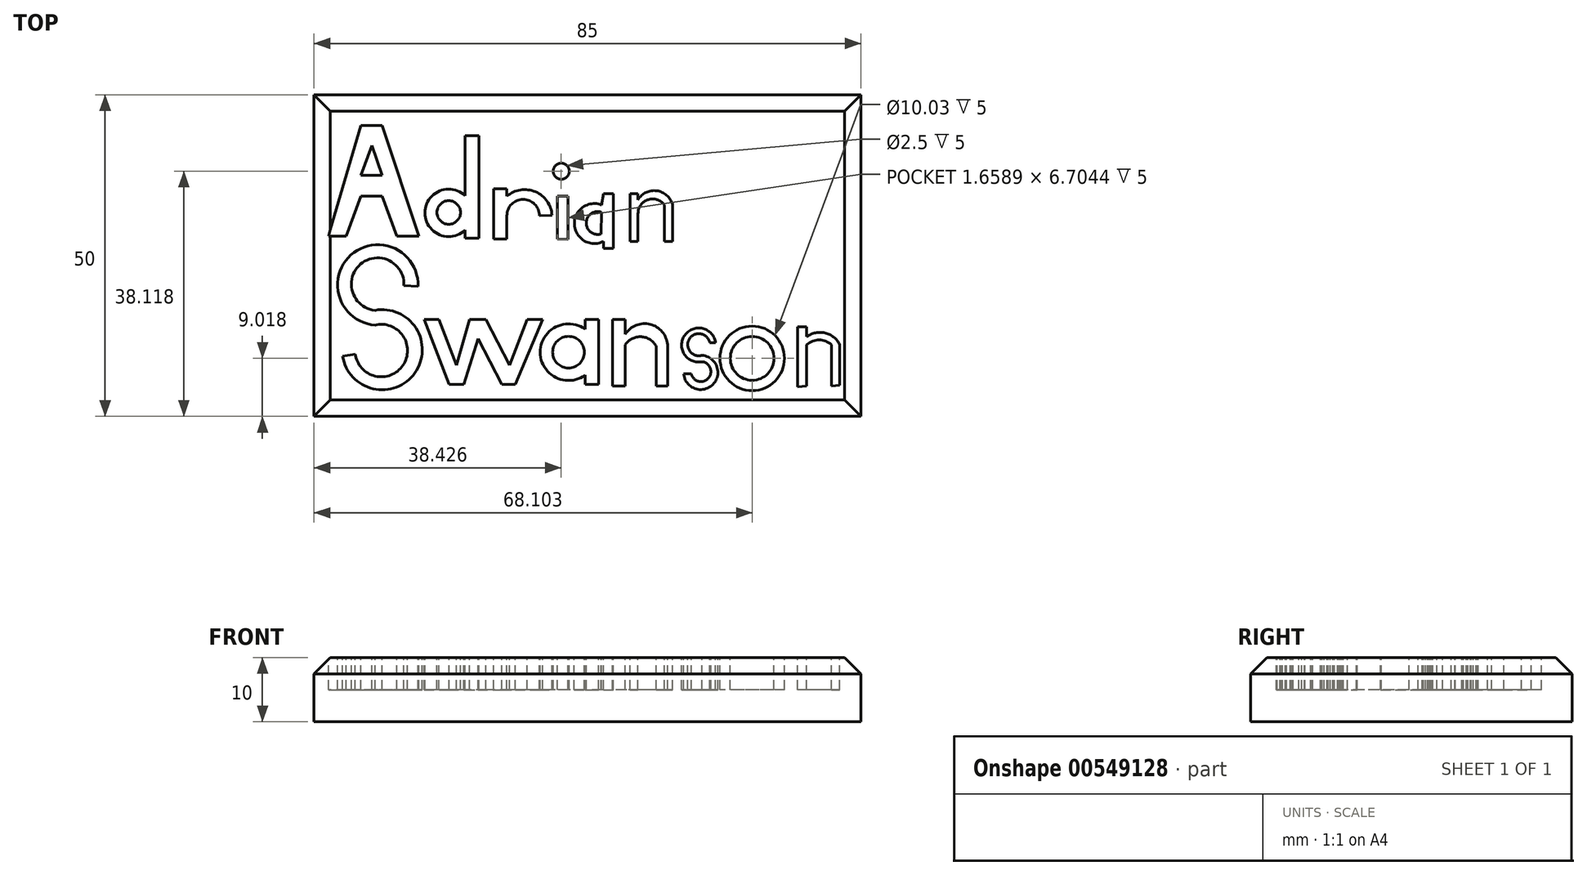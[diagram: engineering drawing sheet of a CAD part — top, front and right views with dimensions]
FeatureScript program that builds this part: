
annotation { "Feature Type Name" : "Feature", "Feature Type Description" : "" }
export const myFeature = defineFeature(function(context is Context, id is Id, definition is map)
    precondition{}
    {
        {
            var Q0;
            Q0=qCreatedBy(makeId("Top.planeOp"),FACE);
            var sketch = newSketch(context, id + "F0", { "sketchPlane" : qUnion([Q0])});
            skLineSegment(sketch, "E0", {"start": v(-29.18, 47.31) * mm, "end": v(55.82, 47.31) * mm});
            skLineSegment(sketch, "E1", {"start": v(-29.18, 47.31) * mm, "end": v(-29.18, -2.69) * mm});
            skLineSegment(sketch, "E2", {"start": v(55.82, 47.31) * mm, "end": v(55.82, -2.69) * mm});
            skLineSegment(sketch, "E3", {"start": v(-29.18, -2.69) * mm, "end": v(55.82, -2.69) * mm});
            skSolve(sketch);
        }
        {
            var Q0;
            Q0 = qSketchRegion(id + "F0", true);
            extrude(context, id + "F1", {"entities" : qUnion([Q0]), "depth" : 10 * mm, "offsetDistance" : 25.4 * mm});
        }
        {
            var Q0;
            Q0=makeQuery(id+"F1.opExtrude","CAP_FACE",FACE,{"disambiguationData":[OSD([sQuery(id+"F0.wireOp",EDGE,"E0"),sQuery(id+"F0.wireOp",EDGE,"E1"),sQuery(id+"F0.wireOp",EDGE,"E2"),sQuery(id+"F0.wireOp",EDGE,"E3")])],"isStart":false});
            var sketch = newSketch(context, id + "F2", { "sketchPlane" : qUnion([Q0])});
            skLineSegment(sketch, "E4", {"start": v(-26.94, 25.33) * mm, "end": v(-24.2, 25.33) * mm});
            skLineSegment(sketch, "E5", {"start": v(-24.2, 25.33) * mm, "end": v(-21.92, 31.56) * mm});
            skLineSegment(sketch, "E6", {"start": v(-21.92, 31.56) * mm, "end": v(-18.62, 31.56) * mm});
            skLineSegment(sketch, "E7", {"start": v(-18.62, 31.56) * mm, "end": v(-16.34, 25.33) * mm});
            skLineSegment(sketch, "E8", {"start": v(-16.34, 25.33) * mm, "end": v(-12.91, 25.33) * mm});
            skLineSegment(sketch, "E9", {"start": v(-12.91, 25.33) * mm, "end": v(-18.62, 42.52) * mm});
            skLineSegment(sketch, "E10", {"start": v(-18.62, 42.52) * mm, "end": v(-21.92, 42.52) * mm});
            skLineSegment(sketch, "E11", {"start": v(-21.92, 42.52) * mm, "end": v(-26.94, 25.33) * mm});
            skLineSegment(sketch, "E12", {"start": v(-18.62, 34.8) * mm, "end": v(-21.92, 34.8) * mm});
            skLineSegment(sketch, "E13", {"start": v(-21.92, 34.8) * mm, "end": v(-20.2, 39.41) * mm});
            skLineSegment(sketch, "E14", {"start": v(-20.2, 39.41) * mm, "end": v(-18.62, 34.8) * mm});
            skCircle(sketch, "E15", {"center": v(-8.25, 29) * mm, "radius": 1.83 * mm});
            skLineSegment(sketch, "E16", {"start": v(-5.68, 26.27) * mm, "end": v(-5.68, 25.02) * mm});
            skLineSegment(sketch, "E17", {"start": v(-5.68, 25.02) * mm, "end": v(-3.56, 25.02) * mm});
            skLineSegment(sketch, "E18", {"start": v(-3.56, 25.02) * mm, "end": v(-3.56, 40.93) * mm});
            skLineSegment(sketch, "E19", {"start": v(-3.56, 40.93) * mm, "end": v(-5.68, 40.93) * mm});
            skLineSegment(sketch, "E20", {"start": v(-5.68, 40.93) * mm, "end": v(-5.68, 31.62) * mm});
            skArc(sketch, "E21", {"start": v(-5.68, 31.62) * mm, "mid": v(-11.94, 28.95) * mm, "end": v(-5.68, 26.27) * mm});
            skLineSegment(sketch, "E22", {"start": v(-1.25, 24.89) * mm, "end": v(0.8, 24.89) * mm});
            skLineSegment(sketch, "E23", {"start": v(0.8, 24.89) * mm, "end": v(0.8, 28.52) * mm});
            skLineSegment(sketch, "E24", {"start": v(-1.25, 24.89) * mm, "end": v(-1.25, 32.68) * mm});
            skLineSegment(sketch, "E25", {"start": v(-1.25, 32.68) * mm, "end": v(0.8, 32.68) * mm});
            skLineSegment(sketch, "E26", {"start": v(0.8, 32.68) * mm, "end": v(0.8, 31.52) * mm});
            skArc(sketch, "E27", {"start": v(5.85, 28.52) * mm, "mid": v(3.32, 31.05) * mm, "end": v(0.8, 28.52) * mm});
            skArc(sketch, "E28", {"start": v(7.8, 28.54) * mm, "mid": v(5.23, 32.22) * mm, "end": v(0.8, 31.52) * mm});
            skLineSegment(sketch, "E29", {"start": v(5.85, 28.52) * mm, "end": v(7.8, 28.54) * mm});
            skLineSegment(sketch, "E30", {"start": v(8.63, 31.56) * mm, "end": v(8.63, 24.89) * mm});
            skLineSegment(sketch, "E31", {"start": v(8.63, 24.89) * mm, "end": v(10.29, 24.85) * mm});
            skLineSegment(sketch, "E32", {"start": v(10.29, 24.85) * mm, "end": v(10.29, 31.56) * mm});
            skLineSegment(sketch, "E33", {"start": v(10.29, 31.56) * mm, "end": v(8.63, 31.56) * mm});
            skCircle(sketch, "E34", {"center": v(9.25, 35.43) * mm, "radius": 1.25 * mm});
            skArc(sketch, "E35", {"start": v(15.52, 30.18) * mm, "mid": v(11.28, 27.12) * mm, "end": v(15.83, 24.53) * mm});
            skArc(sketch, "E36", {"start": v(15.52, 29.05) * mm, "mid": v(13.14, 27.43) * mm, "end": v(15.42, 25.66) * mm});
            skLineSegment(sketch, "E37", {"start": v(15.52, 29.05) * mm, "end": v(15.42, 25.66) * mm});
            skLineSegment(sketch, "E38", {"start": v(15.83, 24.53) * mm, "end": v(15.83, 23.4) * mm});
            skLineSegment(sketch, "E39", {"start": v(15.83, 23.4) * mm, "end": v(17.37, 23.4) * mm});
            skLineSegment(sketch, "E40", {"start": v(17.37, 23.4) * mm, "end": v(17.37, 31.93) * mm});
            skLineSegment(sketch, "E41", {"start": v(17.37, 31.93) * mm, "end": v(15.83, 31.93) * mm});
            skLineSegment(sketch, "E42", {"start": v(15.83, 31.93) * mm, "end": v(15.52, 30.18) * mm});
            skLineSegment(sketch, "E43", {"start": v(19.94, 31.93) * mm, "end": v(19.94, 24.53) * mm});
            skLineSegment(sketch, "E44", {"start": v(19.94, 24.53) * mm, "end": v(21.18, 24.53) * mm});
            skLineSegment(sketch, "E45", {"start": v(21.18, 24.53) * mm, "end": v(21.18, 28.85) * mm});
            skLineSegment(sketch, "E46", {"start": v(19.94, 31.93) * mm, "end": v(21.18, 31.93) * mm});
            skLineSegment(sketch, "E47", {"start": v(21.18, 31.93) * mm, "end": v(21.18, 31) * mm});
            skArc(sketch, "E48", {"start": v(26.52, 30.29) * mm, "mid": v(24.08, 32.38) * mm, "end": v(21.18, 31) * mm});
            skArc(sketch, "E49", {"start": v(25.29, 30.18) * mm, "mid": v(22.75, 31) * mm, "end": v(21.18, 28.85) * mm});
            skLineSegment(sketch, "E50", {"start": v(25.29, 30.18) * mm, "end": v(25.29, 24.53) * mm});
            skLineSegment(sketch, "E51", {"start": v(25.29, 24.53) * mm, "end": v(26.52, 24.53) * mm});
            skLineSegment(sketch, "E52", {"start": v(26.52, 24.53) * mm, "end": v(26.52, 30.29) * mm});
            skSolve(sketch);
        }
        {
            var Q0;
            Q0=makeQuery(id+"F1.opExtrude","CAP_FACE",FACE,{"disambiguationData":[OSD([sQuery(id+"F0.wireOp",EDGE,"E0"),sQuery(id+"F0.wireOp",EDGE,"E1"),sQuery(id+"F0.wireOp",EDGE,"E2"),sQuery(id+"F0.wireOp",EDGE,"E3")])],"isStart":false});
            var sketch = newSketch(context, id + "F3", { "sketchPlane" : qUnion([Q0])});
            skArc(sketch, "E53", {"start": v(-13.02, 17.53) * mm, "mid": v(-23.46, 22.38) * mm, "end": v(-19.7, 11.5) * mm});
            skArc(sketch, "E54", {"start": v(-15.21, 17.64) * mm, "mid": v(-21.95, 20.98) * mm, "end": v(-19.7, 13.8) * mm});
            skArc(sketch, "E55", {"start": v(-24.75, 6.68) * mm, "mid": v(-13.5, 4.07) * mm, "end": v(-19.7, 13.8) * mm});
            skArc(sketch, "E56", {"start": v(-22.77, 7) * mm, "mid": v(-15.36, 5.24) * mm, "end": v(-19.7, 11.5) * mm});
            skLineSegment(sketch, "E57", {"start": v(-12.03, 12.38) * mm, "end": v(-8.2, 2.3) * mm});
            skLineSegment(sketch, "E58", {"start": v(-8.2, 2.3) * mm, "end": v(-5.9, 2.3) * mm});
            skLineSegment(sketch, "E59", {"start": v(-5.9, 2.3) * mm, "end": v(-3.7, 9.42) * mm});
            skLineSegment(sketch, "E60", {"start": v(-3.7, 9.42) * mm, "end": v(0, 2.3) * mm});
            skLineSegment(sketch, "E61", {"start": v(0, 2.3) * mm, "end": v(2.1, 2.3) * mm});
            skLineSegment(sketch, "E62", {"start": v(2.1, 2.3) * mm, "end": v(6.38, 12.38) * mm});
            skLineSegment(sketch, "E63", {"start": v(6.38, 12.38) * mm, "end": v(3.97, 12.38) * mm});
            skLineSegment(sketch, "E64", {"start": v(3.97, 12.38) * mm, "end": v(1.23, 5.25) * mm});
            skLineSegment(sketch, "E65", {"start": v(1.23, 5.25) * mm, "end": v(-2.48, 12.38) * mm});
            skLineSegment(sketch, "E66", {"start": v(-2.48, 12.38) * mm, "end": v(-5.02, 12.38) * mm});
            skLineSegment(sketch, "E67", {"start": v(-5.02, 12.38) * mm, "end": v(-7.05, 5.25) * mm});
            skPoint(sketch, "E67.endSnap0", {"position": v(-7.05, 2.3) * mm});
            skLineSegment(sketch, "E68", {"start": v(-7.05, 5.25) * mm, "end": v(-9.76, 12.38) * mm});
            skLineSegment(sketch, "E69", {"start": v(-9.76, 12.38) * mm, "end": v(-12.03, 12.38) * mm});
            skLineSegment(sketch, "E70", {"start": v(-15.21, 17.64) * mm, "end": v(-13.02, 17.53) * mm});
            skLineSegment(sketch, "E71", {"start": v(-22.77, 7) * mm, "end": v(-24.75, 6.68) * mm});
            skLineSegment(sketch, "E72", {"start": v(15.04, 12.38) * mm, "end": v(15.04, 2.3) * mm});
            skLineSegment(sketch, "E73", {"start": v(15.04, 2.3) * mm, "end": v(12.95, 2.3) * mm});
            skLineSegment(sketch, "E74", {"start": v(12.95, 2.3) * mm, "end": v(12.95, 3.72) * mm});
            skLineSegment(sketch, "E75", {"start": v(12.95, 10.84) * mm, "end": v(12.95, 12.38) * mm});
            skLineSegment(sketch, "E76", {"start": v(12.95, 12.38) * mm, "end": v(15.04, 12.38) * mm});
            skArc(sketch, "E77", {"start": v(12.95, 10.84) * mm, "mid": v(5.97, 7.28) * mm, "end": v(12.95, 3.72) * mm});
            skCircle(sketch, "E78", {"center": v(10.37, 7.28) * mm, "radius": 2.47 * mm});
            skLineSegment(sketch, "E79", {"start": v(17.23, 12.38) * mm, "end": v(17.23, 2.03) * mm});
            skLineSegment(sketch, "E80", {"start": v(17.23, 2.03) * mm, "end": v(19.2, 2.03) * mm});
            skLineSegment(sketch, "E81", {"start": v(19.2, 2.03) * mm, "end": v(19.2, 8.45) * mm});
            skLineSegment(sketch, "E82", {"start": v(19.2, 10.08) * mm, "end": v(19.2, 12.38) * mm});
            skLineSegment(sketch, "E83", {"start": v(19.2, 12.38) * mm, "end": v(17.23, 12.38) * mm});
            skArc(sketch, "E84", {"start": v(25.76, 8.45) * mm, "mid": v(23.07, 11.63) * mm, "end": v(19.2, 10.08) * mm});
            skArc(sketch, "E85", {"start": v(24.02, 8.17) * mm, "mid": v(21.7, 9.69) * mm, "end": v(19.2, 8.45) * mm});
            skLineSegment(sketch, "E86", {"start": v(24.02, 8.17) * mm, "end": v(24.02, 2.03) * mm});
            skLineSegment(sketch, "E87", {"start": v(24.02, 2.03) * mm, "end": v(25.76, 2.03) * mm});
            skLineSegment(sketch, "E88", {"start": v(25.76, 2.03) * mm, "end": v(25.76, 8.45) * mm});
            skArc(sketch, "E89", {"start": v(33.23, 8.76) * mm, "mid": v(28.44, 9.92) * mm, "end": v(31.15, 5.8) * mm});
            skArc(sketch, "E90", {"start": v(32.33, 8.76) * mm, "mid": v(29.16, 9.34) * mm, "end": v(31.15, 6.8) * mm});
            skArc(sketch, "E91", {"start": v(28.27, 3.91) * mm, "mid": v(32.81, 2.26) * mm, "end": v(31.15, 6.8) * mm});
            skArc(sketch, "E92", {"start": v(29.44, 3.91) * mm, "mid": v(32.1, 3.23) * mm, "end": v(31.15, 5.8) * mm});
            skLineSegment(sketch, "E93", {"start": v(32.33, 8.76) * mm, "end": v(33.23, 8.76) * mm});
            skLineSegment(sketch, "E94", {"start": v(28.27, 3.91) * mm, "end": v(29.44, 3.91) * mm});
            skCircle(sketch, "E95", {"center": v(38.92, 6.33) * mm, "radius": 5.01 * mm});
            skCircle(sketch, "E96", {"center": v(38.92, 6.33) * mm, "radius": 3.4 * mm});
            skLineSegment(sketch, "E97", {"start": v(47.4, 2.03) * mm, "end": v(45.98, 1.9) * mm});
            skLineSegment(sketch, "E98", {"start": v(45.98, 1.9) * mm, "end": v(45.98, 11.23) * mm});
            skPoint(sketch, "E98.endSnap0", {"position": v(19.2, 11.23) * mm});
            skLineSegment(sketch, "E99", {"start": v(45.98, 11.23) * mm, "end": v(47.4, 11.2) * mm});
            skLineSegment(sketch, "E100", {"start": v(47.4, 11.2) * mm, "end": v(47.4, 9.68) * mm});
            skLineSegment(sketch, "E101", {"start": v(47.4, 8.45) * mm, "end": v(47.4, 2.03) * mm});
            skArc(sketch, "E102", {"start": v(52.54, 8.45) * mm, "mid": v(50.26, 10.27) * mm, "end": v(47.4, 9.68) * mm});
            skArc(sketch, "E103", {"start": v(51.25, 8.45) * mm, "mid": v(49.33, 9.18) * mm, "end": v(47.4, 8.45) * mm});
            skLineSegment(sketch, "E104", {"start": v(51.25, 8.45) * mm, "end": v(51.25, 2.03) * mm});
            skLineSegment(sketch, "E105", {"start": v(51.25, 2.03) * mm, "end": v(52.54, 2.14) * mm});
            skLineSegment(sketch, "E106", {"start": v(52.54, 2.14) * mm, "end": v(52.54, 8.45) * mm});
            skSolve(sketch);
        }
        {
            var Q0;
            Q0=makeQuery(id+"F1.opExtrude","CAP_FACE",FACE,{"disambiguationData":[OSD([sQuery(id+"F0.wireOp",EDGE,"E0"),sQuery(id+"F0.wireOp",EDGE,"E1"),sQuery(id+"F0.wireOp",EDGE,"E2"),sQuery(id+"F0.wireOp",EDGE,"E3")])],"isStart":false});
            chamfer(context, id + "F4", {"entities" : qUnion([Q0]), "width" : 2.54 * mm, "tangentPropagation" : true});
        }
        {
            var Q0;
            Q0 = qSketchRegion(id + "F2", true);
            var Q1;
            Q1 = qSketchRegion(id + "F3", true);
            extrude(context, id + "F5", {"entities" : qUnion([Q0, Q1]), "operationType" : NewBodyOperationType.REMOVE, "oppositeDirection" : true, "depth" : 5 * mm, "offsetDistance" : 25.4 * mm});
        }
    });
